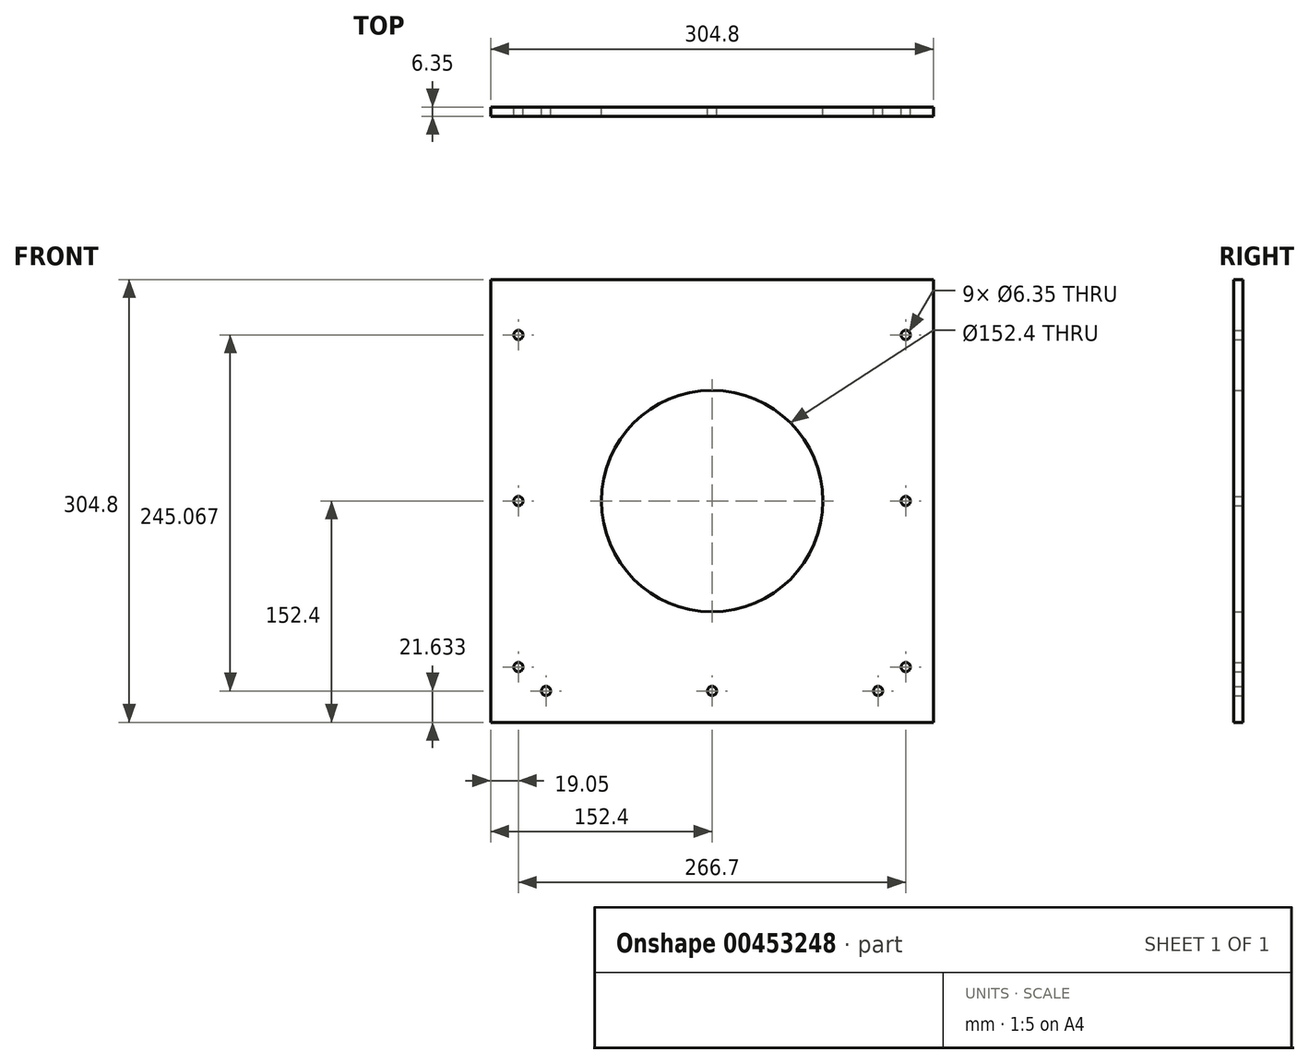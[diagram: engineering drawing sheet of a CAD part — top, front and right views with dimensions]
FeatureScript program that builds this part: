
annotation { "Feature Type Name" : "Feature", "Feature Type Description" : "" }
export const myFeature = defineFeature(function(context is Context, id is Id, definition is map)
    precondition{}
    {
        {
            var Q0;
            Q0=qCreatedBy(makeId("Front.planeOp"),FACE);
            var sketch = newSketch(context, id + "F0", { "sketchPlane" : qUnion([Q0])});
            skLineSegment(sketch, "E0.bottom", {"start": v(-152.4, 152.4) * mm, "end": v(152.4, 152.4) * mm});
            skLineSegment(sketch, "E0.top", {"start": v(-152.4, -152.4) * mm, "end": v(152.4, -152.4) * mm});
            skLineSegment(sketch, "E0.left", {"start": v(-152.4, 152.4) * mm, "end": v(-152.4, -152.4) * mm});
            skLineSegment(sketch, "E0.right", {"start": v(152.4, 152.4) * mm, "end": v(152.4, -152.4) * mm});
            skPoint(sketch, "E0.middle", {"position": v(0, 0) * mm});
            skCircle(sketch, "E1", {"center": v(0, 0) * mm, "radius": 76.2 * mm});
            skPoint(sketch, "E2", {"position": v(-114.3, 152.4) * mm});
            skPoint(sketch, "E3", {"position": v(114.3, 152.4) * mm});
            skPoint(sketch, "E4", {"position": v(152.4, -114.3) * mm});
            skPoint(sketch, "E5", {"position": v(-152.4, -114.3) * mm});
            skPoint(sketch, "E6", {"position": v(0, -114.3) * mm});
            skPoint(sketch, "E7", {"position": v(-152.4, -152.4) * mm});
            skPoint(sketch, "E8", {"position": v(152.4, -152.4) * mm});
            skPoint(sketch, "E9", {"position": v(0, -130.77) * mm});
            skPoint(sketch, "E9.positionSnap0", {"position": v(0, -152.4) * mm});
            skPoint(sketch, "E10", {"position": v(114.3, -114.3) * mm});
            skPoint(sketch, "E11", {"position": v(133.35, 152.4) * mm});
            skPoint(sketch, "E12", {"position": v(-152.4, 152.4) * mm});
            skPoint(sketch, "E13", {"position": v(-133.35, 152.4) * mm});
            skPoint(sketch, "E14", {"position": v(-133.35, 114.3) * mm});
            skPoint(sketch, "E15", {"position": v(133.35, 114.3) * mm});
            skPoint(sketch, "E16", {"position": v(-133.35, 0) * mm});
            skPoint(sketch, "E17", {"position": v(133.35, 0) * mm});
            skPoint(sketch, "E17.positionSnap0", {"position": v(114.3, 0) * mm});
            skPoint(sketch, "E18", {"position": v(133.35, -114.3) * mm});
            skPoint(sketch, "E19", {"position": v(114.3, -130.77) * mm});
            skPoint(sketch, "E20", {"position": v(-114.3, -130.77) * mm});
            skPoint(sketch, "E21", {"position": v(-133.35, -114.3) * mm});
            skPoint(sketch, "E22.orphan", {"position": v(114.3, -152.4) * mm});
            skSolve(sketch);
        }
        {
            var Q0;
            Q0=makeQuery(id+"F0.imprint","IMPRINT",FACE,{"disambiguationData":[TD([[makeQuery(id+"F0.imprint","IMPRINT",EDGE,{"derivedFrom":sQuery(id+"F0.wireOp",EDGE,"E0.top")}),1.0]])]});
            var Q1;
            Q1=makeQuery(id+"F0.imprint","IMPRINT",FACE,{"disambiguationData":[TD([[makeQuery(id+"F0.imprint","IMPRINT",EDGE,{"derivedFrom":sQuery(id+"F0.wireOp",EDGE,"E1")}),-1.0]])]});
            extrude(context, id + "F1", {"entities" : qUnion([Q0, Q1]), "depth" : 6.35 * mm});
        }
        {
            var Q0;
            Q0=sQuery(id+"F0.wireOp",VERTEX,"E14");
            var Q1;
            Q1=sQuery(id+"F0.wireOp",VERTEX,"E16");
            var Q2;
            Q2=sQuery(id+"F0.wireOp",VERTEX,"E15");
            var Q3;
            Q3=sQuery(id+"F0.wireOp",VERTEX,"E17");
            var Q4;
            Q4=sQuery(id+"F0.wireOp",VERTEX,"E18");
            var Q5;
            Q5=sQuery(id+"F0.wireOp",VERTEX,"E19");
            var Q6;
            Q6=sQuery(id+"F0.wireOp",VERTEX,"E9");
            var Q7;
            Q7=sQuery(id+"F0.wireOp",VERTEX,"E20");
            var Q8;
            Q8=sQuery(id+"F0.wireOp",VERTEX,"E21");
            var Q9;
            Q9=makeQuery(id+"F1.opExtrude","SWEPT_BODY",BODY,{"disambiguationData":[OSD([sQuery(id+"F0.wireOp",EDGE,"E0.bottom"),sQuery(id+"F0.wireOp",EDGE,"E0.top"),sQuery(id+"F0.wireOp",EDGE,"E0.left"),sQuery(id+"F0.wireOp",EDGE,"E0.right"),sQuery(id+"F0.wireOp",EDGE,"AaP693tJ-aY9V-Gg4H-F7cB-QEXXz2j3KlHL"),sQuery(id+"F0.wireOp",EDGE,"2kTmDERm-w5ZB-NTXp-iEBD-sCiNr6YcPeEY"),sQuery(id+"F0.wireOp",EDGE,"XhKL7dPE-ChZL-5iVZ-jEm2-Fz3PHWsSEwdd")])]});
            hole(context, id + "F2", {"style" : HoleStyle.C_BORE, "endStyle" : HoleEndStyle.BLIND, "oppositeDirection" : true, "holeDiameter" : 6.35 * mm, "cBoreDiameter" : 6.35 * mm, "cBoreDepth" : 304.8 * mm, "holeDepth" : 304.8 * mm, "isTappedThrough" : true, "tappedDepth" : 12.7 * mm, "tapClearance" : 3, "startFromSketch" : true, "locations" : qUnion([Q0, Q1, Q2, Q3, Q4, Q5, Q6, Q7, Q8]), "scope" : qUnion([Q9])});
        }
    });
